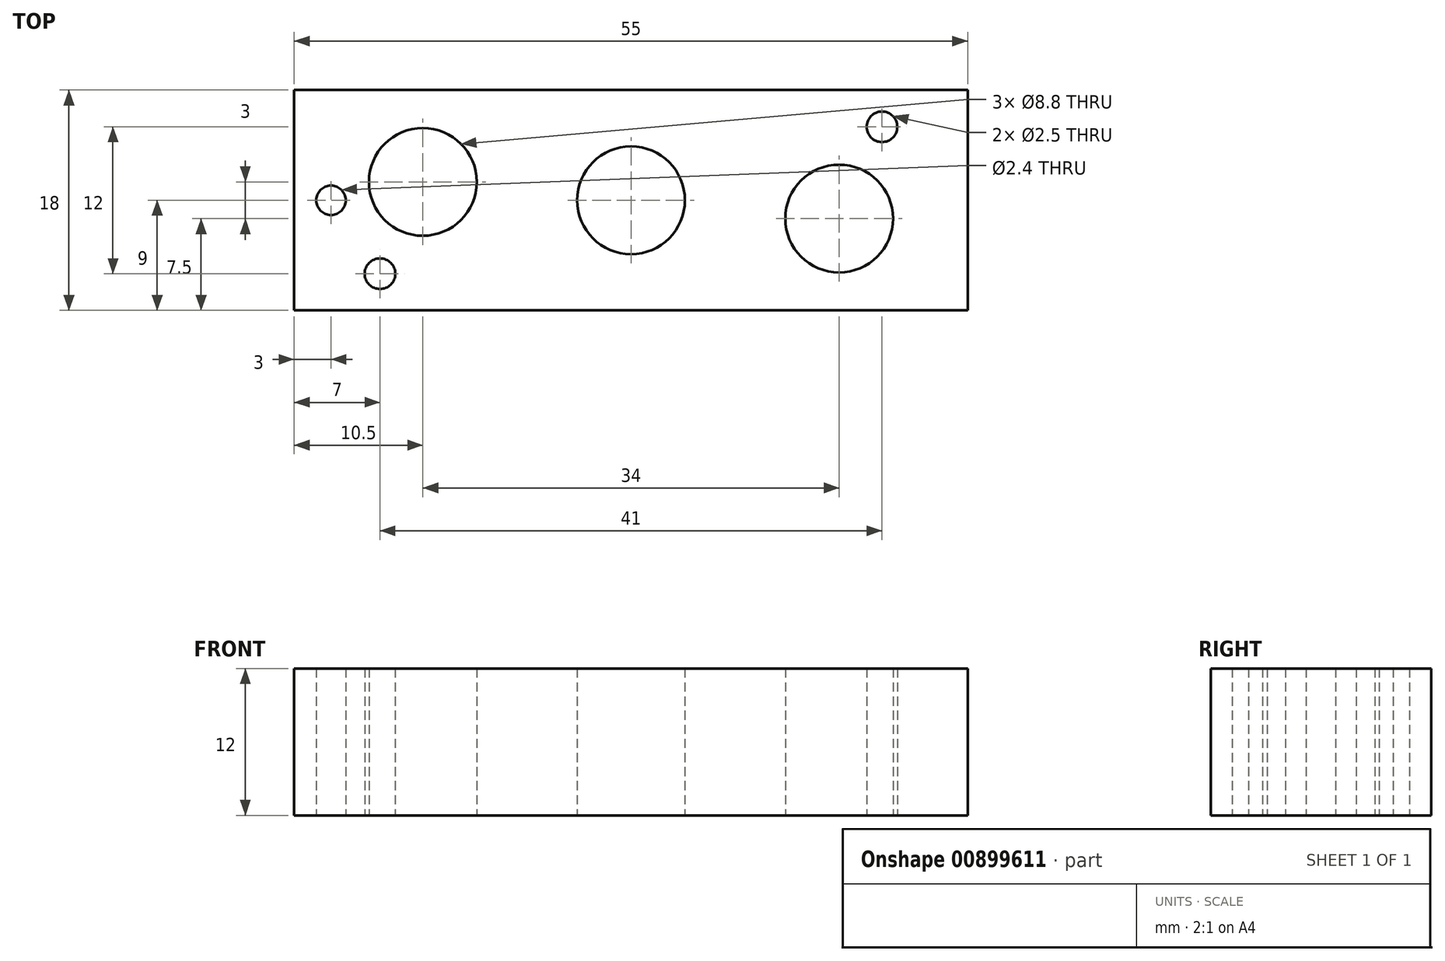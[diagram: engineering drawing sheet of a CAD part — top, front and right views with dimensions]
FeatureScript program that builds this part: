
annotation { "Feature Type Name" : "Feature", "Feature Type Description" : "" }
export const myFeature = defineFeature(function(context is Context, id is Id, definition is map)
    precondition{}
    {
        {
            var Q0;
            Q0=qCreatedBy(makeId("Top.planeOp"),FACE);
            var sketch = newSketch(context, id + "F0", { "sketchPlane" : qUnion([Q0])});
            skLineSegment(sketch, "E0.bottom", {"start": v(27.5, 9) * mm, "end": v(-27.5, 9) * mm});
            skLineSegment(sketch, "E0.top", {"start": v(27.5, -9) * mm, "end": v(-27.5, -9) * mm});
            skLineSegment(sketch, "E0.left", {"start": v(27.5, 9) * mm, "end": v(27.5, -9) * mm});
            skLineSegment(sketch, "E0.right", {"start": v(-27.5, 9) * mm, "end": v(-27.5, -9) * mm});
            skPoint(sketch, "E0.middle", {"position": v(0, 0) * mm});
            skCircle(sketch, "E1", {"center": v(0, 0) * mm, "radius": 4.4 * mm});
            skCircle(sketch, "E2", {"center": v(17, -1.5) * mm, "radius": 4.4 * mm});
            skCircle(sketch, "E3", {"center": v(-17, 1.5) * mm, "radius": 4.4 * mm});
            skLineSegment(sketch, "E4", {"start": v(-27.5, 0) * mm, "end": v(27.5, 0) * mm, "construction": true});
            skLineSegment(sketch, "E5", {"start": v(0, -9) * mm, "end": v(0, 9) * mm, "construction": true});
            skCircle(sketch, "E6", {"center": v(20.5, 6) * mm, "radius": 1.25 * mm});
            skCircle(sketch, "E7", {"center": v(-20.5, -6) * mm, "radius": 1.25 * mm});
            skCircle(sketch, "E8", {"center": v(-24.5, 0) * mm, "radius": 1.2 * mm});
            skSolve(sketch);
        }
        {
            var Q0;
            Q0=makeQuery(id+"F0.imprint","IMPRINT",FACE,{"disambiguationData":[TD([[makeQuery(id+"F0.imprint","IMPRINT",EDGE,{"derivedFrom":sQuery(id+"F0.wireOp",EDGE,"E0.bottom")}),1.0]])]});
            extrude(context, id + "F1", {"entities" : qUnion([Q0]), "depth" : 12 * mm, "offsetDistance" : 25 * mm});
        }
    });
